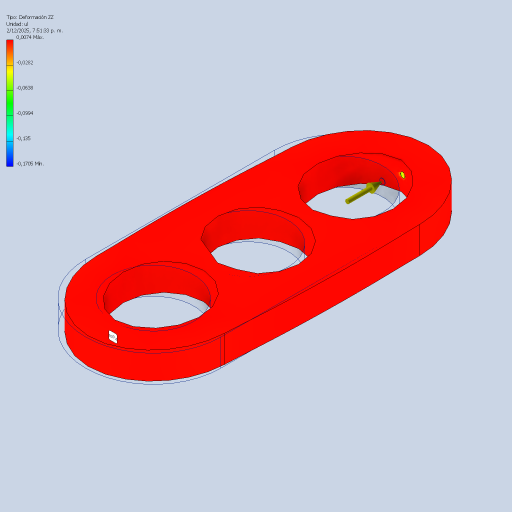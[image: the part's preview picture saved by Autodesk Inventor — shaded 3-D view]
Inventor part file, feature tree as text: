
AUTODESK INVENTOR PART (.ipt)
format: ipt  version: 2024 (Build 280153000, 153)  size: 335,872 bytes
history: native  units: mm
features: sketch x4, other x4, extrude x3, plane x3
ambient origin geometry x8: Origin, YZ Plane, XZ Plane, XY Plane, X Axis, Y Axis, Z Axis, Center Point
bodies: Body1 (feature_tree)
feature tree (14):
  extrude  "Extrusión3"  Depth=10.0mm
  plane  "Plano de trabajo1"
  sketch  "Boceto2"  dims[d12=30.0mm d13=10.0mm d14=0.0mm]
  other  "Punto de trabajo1"
  other  "Punto de trabajo2"
  plane  "Plano de trabajo2"
  plane  "Plano de trabajo3"
  extrude  "Extrusión4"  Depth=10.0mm TaperAngle=0.0deg
  extrude  "Extrusión5"  Depth=2.0mm
  sketch  "Boceto1"  dims[d3=10.0mm d6=0.0mm]
  sketch  "Boceto3"  dims[d15=-25.0mm d16=2.0mm]
  sketch  "Boceto4"  dims[d17=0.1mm d18=0.0mm d19=2.0mm d20=0.1mm d21=0.0mm d22=14.3117mm d23=0.75mm d24=20.594885mm d25=0.0625mm d26=0.75mm d27=0.375mm]
  other  "Proyectar aristas de corte1"
  other  "Proyectar aristas de corte2"
